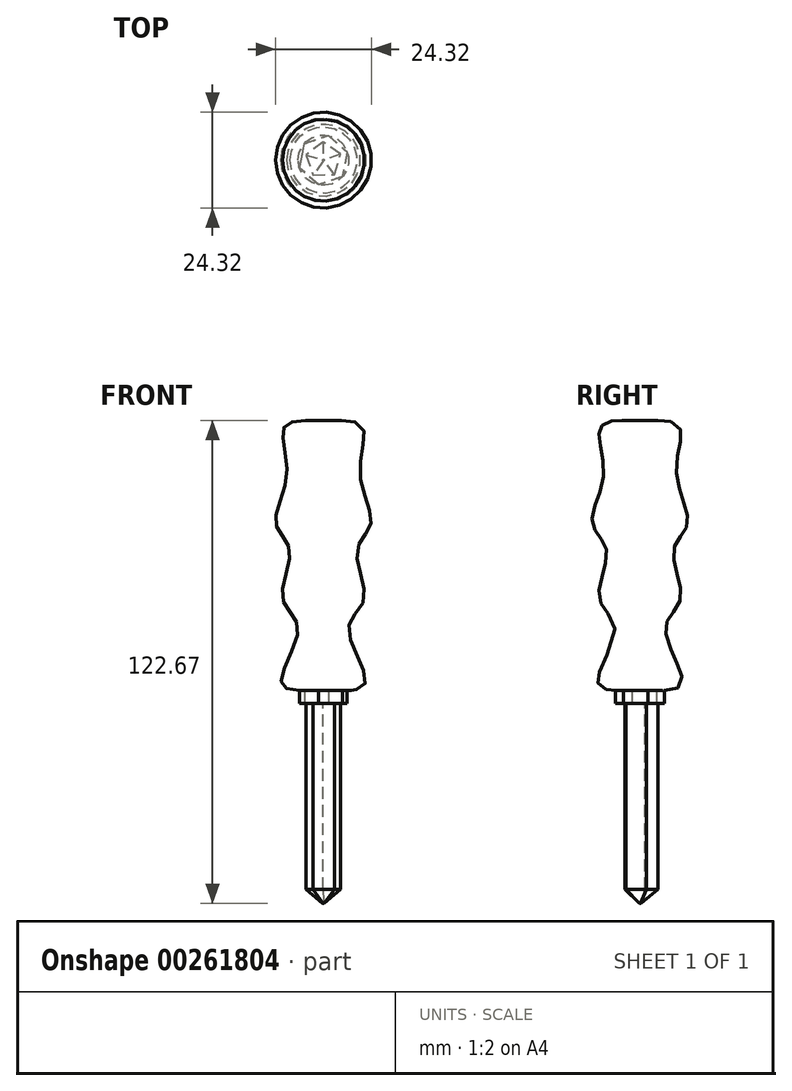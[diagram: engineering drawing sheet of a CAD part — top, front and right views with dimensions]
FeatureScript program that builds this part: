
annotation { "Feature Type Name" : "Feature", "Feature Type Description" : "" }
export const myFeature = defineFeature(function(context is Context, id is Id, definition is map)
    precondition{}
    {
        {
            var Q0;
            Q0=qCreatedBy(makeId("Front.planeOp"),FACE);
            var sketch = newSketch(context, id + "F0", { "sketchPlane" : qUnion([Q0])});
            skLineSegment(sketch, "E0", {"start": v(0, 82.33) * mm, "end": v(0, -81.62) * mm, "construction": true});
            skFitSpline(sketch, "E1", {"points": [v(0, 71.66) * mm, v(-9.96, 70.24) * mm, v(-9.25, 58.5) * mm, v(-12.1, 45.7) * mm, v(-8.54, 38.94) * mm, v(-10.31, 26.5) * mm, v(-6.4, 19.03) * mm, v(-10.67, 5.16) * mm, v(0, 3.73) * mm], "startDerivative": vector(-109.41, 7.47) * mm, "endDerivative": vector(121.63, 12.69) * mm});
            skLineSegment(sketch, "E2", {"start": v(0, 71.66) * mm, "end": v(0, 3.73) * mm});
            skSolve(sketch);
        }
        {
            var Q0;
            Q0 = qSketchRegion(id + "F0", true);
            var Q1;
            Q1=sQuery(id+"F0.wireOp",EDGE,"E0");
            revolve(context, id + "F1", {"entities" : qUnion([Q0]), "axis" : qUnion([Q1]), "revolveType" : RevolveType.FULL});
        }
        {
            var Q0;
            Q0=qCreatedBy(makeId("Top.planeOp"),FACE);
            var sketch = newSketch(context, id + "F2", { "sketchPlane" : qUnion([Q0])});
            skCircle(sketch, "E3.cCircle", {"center": v(0, 0) * mm, "radius": 5.53 * mm, "construction": true});
            skLineSegment(sketch, "E3.0", {"start": v(1.24, 6.26) * mm, "end": v(6.05, 2.06) * mm});
            skLineSegment(sketch, "E3.1", {"start": v(6.05, 2.06) * mm, "end": v(4.8, -4.2) * mm});
            skLineSegment(sketch, "E3.2", {"start": v(4.8, -4.2) * mm, "end": v(-1.24, -6.26) * mm});
            skLineSegment(sketch, "E3.3", {"start": v(-1.24, -6.26) * mm, "end": v(-6.05, -2.06) * mm});
            skLineSegment(sketch, "E3.4", {"start": v(-6.05, -2.06) * mm, "end": v(-4.8, 4.2) * mm});
            skLineSegment(sketch, "E3.5", {"start": v(-4.8, 4.2) * mm, "end": v(1.24, 6.26) * mm});
            skPoint(sketch, "E3.0.midPoint", {"position": v(3.64, 4.16) * mm});
            skSolve(sketch);
        }
        {
            var Q0;
            Q0 = qSketchRegion(id + "F2", true);
            extrude(context, id + "F3", {"entities" : qUnion([Q0]), "operationType" : NewBodyOperationType.ADD, "depth" : 30.48 * mm});
        }
        {
            var Q0;
            Q0=makeQuery(id+"F3.opExtrude","CAP_FACE",FACE,{"disambiguationData":[OSD([sQuery(id+"F2.wireOp",EDGE,"E3.0"),sQuery(id+"F2.wireOp",EDGE,"E3.1"),sQuery(id+"F2.wireOp",EDGE,"E3.2"),sQuery(id+"F2.wireOp",EDGE,"E3.3"),sQuery(id+"F2.wireOp",EDGE,"E3.4"),sQuery(id+"F2.wireOp",EDGE,"E3.5")])],"isStart":true});
            var sketch = newSketch(context, id + "F4", { "sketchPlane" : qUnion([Q0])});
            skCircle(sketch, "E4.cCircle", {"center": v(0, 0) * mm, "radius": 3.74 * mm, "construction": true});
            skLineSegment(sketch, "E4.0", {"start": v(-0.16, -4.62) * mm, "end": v(-4.44, -1.27) * mm});
            skLineSegment(sketch, "E4.1", {"start": v(-4.44, -1.27) * mm, "end": v(-2.58, 3.83) * mm});
            skLineSegment(sketch, "E4.2", {"start": v(-2.58, 3.83) * mm, "end": v(2.85, 3.64) * mm});
            skLineSegment(sketch, "E4.3", {"start": v(2.85, 3.64) * mm, "end": v(4.34, -1.58) * mm});
            skLineSegment(sketch, "E4.4", {"start": v(4.34, -1.58) * mm, "end": v(-0.16, -4.62) * mm});
            skPoint(sketch, "E4.0.midPoint", {"position": v(-2.3, -2.95) * mm});
            skSolve(sketch);
        }
        {
            var Q0;
            Q0 = qSketchRegion(id + "F4", true);
            extrude(context, id + "F5", {"entities" : qUnion([Q0]), "operationType" : NewBodyOperationType.ADD, "depth" : 50.8 * mm});
        }
        {
            var Q0;
            Q0=makeQuery(id+"F5.opExtrude","CAP_EDGE",EDGE,{"disambiguationData":[OSD([sQuery(id+"F4.wireOp",EDGE,"E4.4")])],"isStart":false});
            var Q1;
            Q1=makeQuery(id+"F5.opExtrude","CAP_EDGE",EDGE,{"disambiguationData":[OSD([sQuery(id+"F4.wireOp",EDGE,"E4.0")])],"isStart":false});
            var Q2;
            Q2=makeQuery(id+"F5.opExtrude","CAP_EDGE",EDGE,{"disambiguationData":[OSD([sQuery(id+"F4.wireOp",EDGE,"E4.1")])],"isStart":false});
            var Q3;
            Q3=makeQuery(id+"F5.opExtrude","CAP_EDGE",EDGE,{"disambiguationData":[OSD([sQuery(id+"F4.wireOp",EDGE,"E4.2")])],"isStart":false});
            var Q4;
            Q4=makeQuery(id+"F5.opExtrude","CAP_EDGE",EDGE,{"disambiguationData":[OSD([sQuery(id+"F4.wireOp",EDGE,"E4.3")])],"isStart":false});
            chamfer(context, id + "F6", {"entities" : qUnion([Q0, Q1, Q2, Q3, Q4]), "width" : 3.56 * mm, "tangentPropagation" : true});
        }
    });
